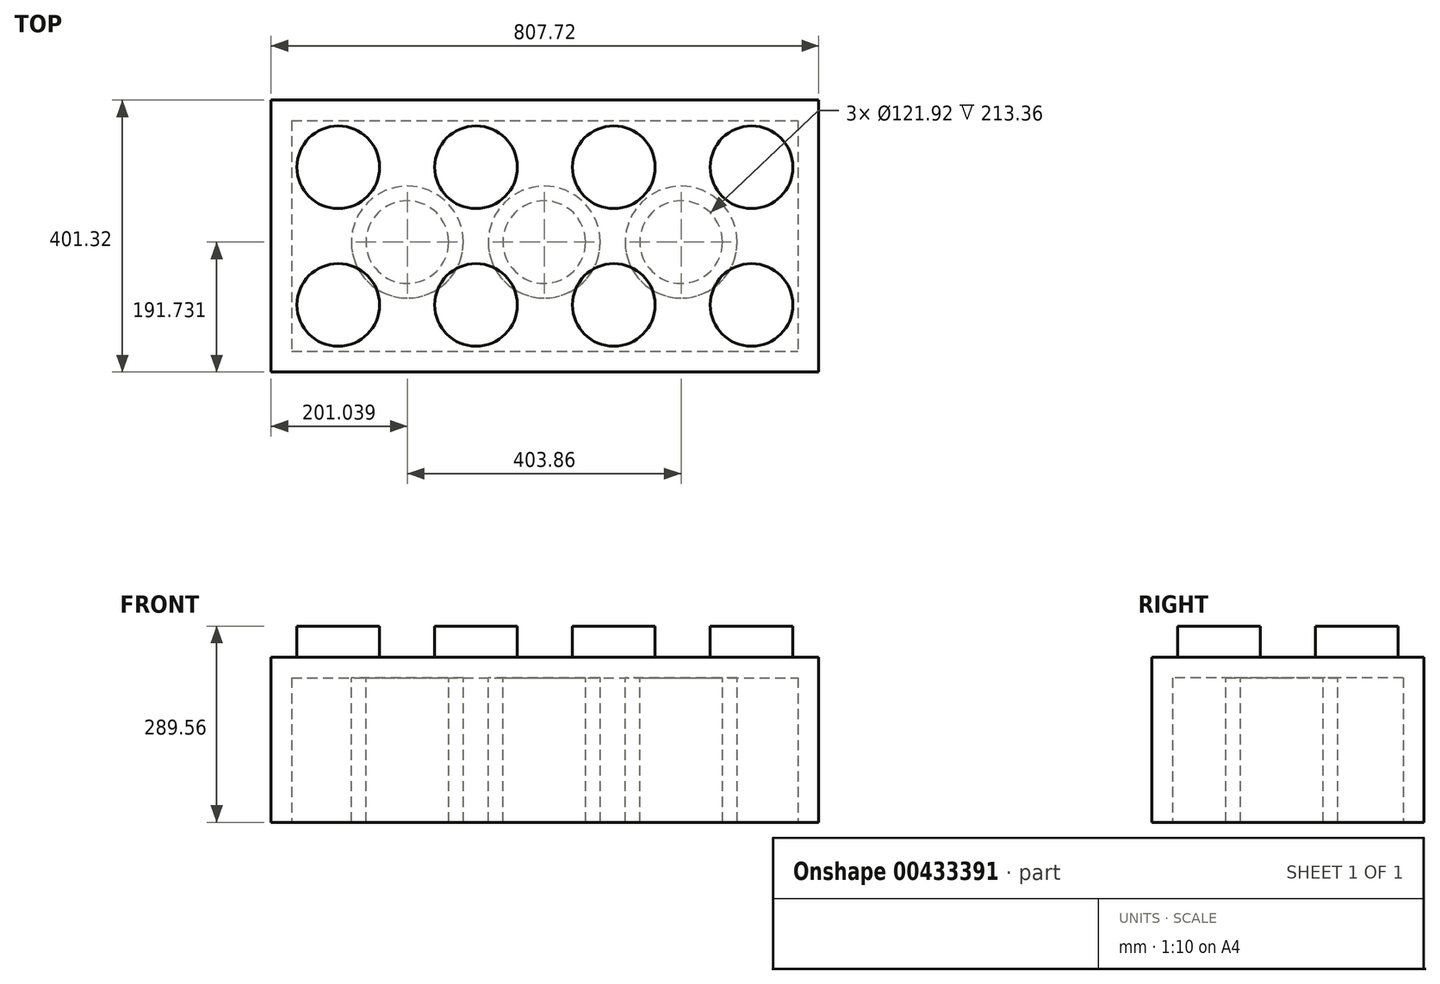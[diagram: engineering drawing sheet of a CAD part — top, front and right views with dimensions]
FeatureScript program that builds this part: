
annotation { "Feature Type Name" : "Feature", "Feature Type Description" : "" }
export const myFeature = defineFeature(function(context is Context, id is Id, definition is map)
    precondition{}
    {
        {
            var Q0;
            Q0=qCreatedBy(makeId("Top.planeOp"),FACE);
            var sketch = newSketch(context, id + "F0", { "sketchPlane" : qUnion([Q0])});
            skLineSegment(sketch, "E0.bottom", {"start": v(-401.62, 149.25) * mm, "end": v(406.1, 149.25) * mm});
            skLineSegment(sketch, "E0.top", {"start": v(-401.62, -252.07) * mm, "end": v(406.1, -252.07) * mm});
            skLineSegment(sketch, "E0.left", {"start": v(-401.62, 149.25) * mm, "end": v(-401.62, -252.07) * mm});
            skLineSegment(sketch, "E0.right", {"start": v(406.1, 149.25) * mm, "end": v(406.1, -252.07) * mm});
            skSolve(sketch);
        }
        {
            var Q0;
            Q0=makeQuery(id+"F0.imprint","IMPRINT",FACE,{"disambiguationData":[TD([[makeQuery(id+"F0.imprint","IMPRINT",EDGE,{"derivedFrom":sQuery(id+"F0.wireOp",EDGE,"E0.bottom")}),-1.0]])]});
            extrude(context, id + "F1", {"entities" : qUnion([Q0]), "depth" : 243.84 * mm});
        }
        {
            var Q0;
            Q0=makeQuery(id+"F1.opExtrude","CAP_FACE",FACE,{"disambiguationData":[OSD([sQuery(id+"F0.wireOp",EDGE,"E0.bottom"),sQuery(id+"F0.wireOp",EDGE,"E0.top"),sQuery(id+"F0.wireOp",EDGE,"E0.left"),sQuery(id+"F0.wireOp",EDGE,"E0.right")])],"isStart":true});
            shell(context, id + "F2", {"entities" : qUnion([Q0]), "thickness" : 30.48 * mm});
        }
        {
            var Q0;
            Q0=makeQuery(id+"F1.opExtrude","CAP_FACE",FACE,{"disambiguationData":[OSD([sQuery(id+"F0.wireOp",EDGE,"E0.bottom"),sQuery(id+"F0.wireOp",EDGE,"E0.top"),sQuery(id+"F0.wireOp",EDGE,"E0.left"),sQuery(id+"F0.wireOp",EDGE,"E0.right")])],"isStart":false});
            var sketch = newSketch(context, id + "F3", { "sketchPlane" : qUnion([Q0])});
            skCircle(sketch, "E1", {"center": v(-302.56, 50.19) * mm, "radius": 60.96 * mm});
            skCircle(sketch, "E2.0.1.0", {"center": v(-302.56, -153.01) * mm, "radius": 60.96 * mm});
            skCircle(sketch, "E2.1.0.0", {"center": v(-99.36, 50.19) * mm, "radius": 60.96 * mm});
            skCircle(sketch, "E2.1.1.0", {"center": v(-99.36, -153.01) * mm, "radius": 60.96 * mm});
            skCircle(sketch, "E2.2.0.0", {"center": v(103.84, 50.19) * mm, "radius": 60.96 * mm});
            skCircle(sketch, "E2.2.1.0", {"center": v(103.84, -153.01) * mm, "radius": 60.96 * mm});
            skCircle(sketch, "E2.3.0.0", {"center": v(307.04, 50.19) * mm, "radius": 60.96 * mm});
            skCircle(sketch, "E2.3.1.0", {"center": v(307.04, -153.01) * mm, "radius": 60.96 * mm});
            skLineSegment(sketch, "E2.direction1", {"start": v(-302.56, 50.19) * mm, "end": v(-99.36, 50.19) * mm, "construction": true});
            skLineSegment(sketch, "E2.direction2", {"start": v(-302.56, 50.19) * mm, "end": v(-302.56, -153.01) * mm, "construction": true});
            skSolve(sketch);
        }
        {
            var Q0;
            Q0 = qSketchRegion(id + "F3", true);
            extrude(context, id + "F4", {"entities" : qUnion([Q0]), "operationType" : NewBodyOperationType.ADD, "depth" : 45.72 * mm});
        }
        {
            var Q0;
            Q0=makeQuery(id+"F2.opShell","OFFSET_FACE",FACE,{"disambiguationData":[OSD([sQuery(id+"F0.wireOp",EDGE,"E0.bottom"),sQuery(id+"F0.wireOp",EDGE,"E0.top"),sQuery(id+"F0.wireOp",EDGE,"E0.left"),sQuery(id+"F0.wireOp",EDGE,"E0.right")])]});
            var sketch = newSketch(context, id + "F5", { "sketchPlane" : qUnion([Q0])});
            skCircle(sketch, "E3", {"center": v(-200.58, 60.34) * mm, "radius": 60.96 * mm});
            skCircle(sketch, "E4", {"center": v(-200.58, 60.34) * mm, "radius": 82.55 * mm});
            skCircle(sketch, "E5.1.0.0", {"center": v(1.35, 60.34) * mm, "radius": 60.96 * mm});
            skCircle(sketch, "E5.1.0.1", {"center": v(1.35, 60.34) * mm, "radius": 82.55 * mm});
            skCircle(sketch, "E5.2.0.0", {"center": v(203.28, 60.34) * mm, "radius": 60.96 * mm});
            skCircle(sketch, "E5.2.0.1", {"center": v(203.28, 60.34) * mm, "radius": 82.55 * mm});
            skLineSegment(sketch, "E5.direction1", {"start": v(-200.58, 60.34) * mm, "end": v(1.35, 60.34) * mm, "construction": true});
            skSolve(sketch);
        }
        {
            var Q0;
            Q0=makeQuery(id+"F5.imprint","IMPRINT",FACE,{"disambiguationData":[TD([[makeQuery(id+"F5.imprint","IMPRINT",EDGE,{"derivedFrom":sQuery(id+"F5.wireOp",EDGE,"E5.2.0.0")}),-1.0]])]});
            var Q1;
            Q1=makeQuery(id+"F5.imprint","IMPRINT",FACE,{"disambiguationData":[TD([[makeQuery(id+"F5.imprint","IMPRINT",EDGE,{"derivedFrom":sQuery(id+"F5.wireOp",EDGE,"E5.1.0.0")}),-1.0]])]});
            var Q2;
            Q2=makeQuery(id+"F5.imprint","IMPRINT",FACE,{"disambiguationData":[TD([[makeQuery(id+"F5.imprint","IMPRINT",EDGE,{"derivedFrom":sQuery(id+"F5.wireOp",EDGE,"E3")}),-1.0]])]});
            extrude(context, id + "F6", {"entities" : qUnion([Q0, Q1, Q2]), "operationType" : NewBodyOperationType.ADD, "depth" : 213.36 * mm});
        }
        {
            var Q0;
            Q0=makeQuery(id+"F1.opExtrude","SWEPT_BODY",BODY,{"disambiguationData":[OSD([sQuery(id+"F0.wireOp",EDGE,"E0.bottom"),sQuery(id+"F0.wireOp",EDGE,"E0.top"),sQuery(id+"F0.wireOp",EDGE,"E0.left"),sQuery(id+"F0.wireOp",EDGE,"E0.right")])]});
            transform(context, id + "F7", {"entities" : qUnion([Q0]), "transformType" : TransformType.TRANSLATION_3D, "dx" : 0 * mm, "dy" : 0 * mm, "dz" : 347.98 * mm, "makeCopy" : true});
        }
        {
            var Q0;
            Q0=makeQuery(id+"F7.opPattern","COPY",BODY,{"derivedFrom":makeQuery(id+"F1.opExtrude","SWEPT_BODY",BODY,{"disambiguationData":[OSD([sQuery(id+"F0.wireOp",EDGE,"E0.bottom"),sQuery(id+"F0.wireOp",EDGE,"E0.top"),sQuery(id+"F0.wireOp",EDGE,"E0.left"),sQuery(id+"F0.wireOp",EDGE,"E0.right")])]}),"instanceName":"1"});
            transform(context, id + "F8", {"entities" : qUnion([Q0]), "transformType" : TransformType.TRANSLATION_3D, "dx" : 0 * mm, "dy" : 0 * mm, "dz" : 548.64 * mm, "makeCopy" : true});
        }
        {
            var Q0;
            Q0=qCreatedBy(makeId("Front.planeOp"),FACE);
            var sketch = newSketch(context, id + "F9", { "sketchPlane" : qUnion([Q0])});
            skLineSegment(sketch, "E6", {"start": v(-791.42, 0) * mm, "end": v(-791.42, 635) * mm});
            skLineSegment(sketch, "E7", {"start": v(-791.42, 635) * mm, "end": v(-1174.33, 635) * mm});
            skLineSegment(sketch, "E8", {"start": v(-1174.33, 635) * mm, "end": v(-840.22, 0) * mm});
            skLineSegment(sketch, "E9", {"start": v(-840.22, 0) * mm, "end": v(-1174.33, -635) * mm});
            skLineSegment(sketch, "E10", {"start": v(-1174.33, -635) * mm, "end": v(-791.42, -635) * mm});
            skLineSegment(sketch, "E11", {"start": v(-791.42, -635) * mm, "end": v(-791.42, 0) * mm});
            skSolve(sketch);
        }
        {
            var Q0;
            Q0=makeQuery(id+"F9.imprint","IMPRINT",FACE,{"disambiguationData":[TD([[makeQuery(id+"F9.imprint","IMPRINT",EDGE,{"derivedFrom":sQuery(id+"F9.wireOp",EDGE,"E6")}),1.0]])]});
            var Q1;
            Q1=sQuery(id+"F9.wireOp",EDGE,"E6");
            revolve(context, id + "F10", {"entities" : qUnion([Q0]), "axis" : qUnion([Q1]), "revolveType" : RevolveType.FULL});
        }
        {
            var Q0;
            Q0=makeQuery(id+"F10.opRevolve","SWEPT_FACE",FACE,{"disambiguationData":[OSD([sQuery(id+"F9.wireOp",EDGE,"E8")])]});
            var Q1;
            Q1=makeQuery(id+"F10.opRevolve","SWEPT_FACE",FACE,{"disambiguationData":[OSD([sQuery(id+"F9.wireOp",EDGE,"E7")])]});
            fillet(context, id + "F11", {"entities" : qUnion([Q0, Q1]), "radius" : 76.2 * mm, "tangentPropagation" : true, "allowEdgeOverflow" : false});
        }
        {
            var Q0;
            Q0=makeQuery(id+"F10.opRevolve","SWEPT_FACE",FACE,{"disambiguationData":[OSD([sQuery(id+"F9.wireOp",EDGE,"E9")])]});
            var Q1;
            Q1=makeQuery(id+"F10.opRevolve","SWEPT_FACE",FACE,{"disambiguationData":[OSD([sQuery(id+"F9.wireOp",EDGE,"E10")])]});
            fillet(context, id + "F12", {"entities" : qUnion([Q0, Q1]), "radius" : 76.2 * mm, "tangentPropagation" : true, "allowEdgeOverflow" : false});
        }
        {
            var Q0;
            Q0=makeQuery(id+"F10.opRevolve","SWEPT_BODY",BODY,{"disambiguationData":[OSD([sQuery(id+"F9.wireOp",EDGE,"E6"),sQuery(id+"F9.wireOp",EDGE,"E7"),sQuery(id+"F9.wireOp",EDGE,"E8"),sQuery(id+"F9.wireOp",EDGE,"E9"),sQuery(id+"F9.wireOp",EDGE,"E10"),sQuery(id+"F9.wireOp",EDGE,"E11")])]});
            deleteBodies(context, id + "F13", {"entities" : qUnion([Q0])});
        }
        {
            var Q0;
            Q0=makeQuery(id+"F8.opPattern","COPY",BODY,{"derivedFrom":makeQuery(id+"F7.opPattern","COPY",BODY,{"derivedFrom":makeQuery(id+"F1.opExtrude","SWEPT_BODY",BODY,{"disambiguationData":[OSD([sQuery(id+"F0.wireOp",EDGE,"E0.bottom"),sQuery(id+"F0.wireOp",EDGE,"E0.top"),sQuery(id+"F0.wireOp",EDGE,"E0.left"),sQuery(id+"F0.wireOp",EDGE,"E0.right")])]}),"instanceName":"1"}),"instanceName":"1"});
            var Q1;
            Q1=makeQuery(id+"F7.opPattern","COPY",BODY,{"derivedFrom":makeQuery(id+"F1.opExtrude","SWEPT_BODY",BODY,{"disambiguationData":[OSD([sQuery(id+"F0.wireOp",EDGE,"E0.bottom"),sQuery(id+"F0.wireOp",EDGE,"E0.top"),sQuery(id+"F0.wireOp",EDGE,"E0.left"),sQuery(id+"F0.wireOp",EDGE,"E0.right")])]}),"instanceName":"1"});
            deleteBodies(context, id + "F14", {"entities" : qUnion([Q0, Q1])});
        }
    });
